# Revit family: M_螢光燈管槽 - 晶體狀
name_source: partatom
category: Leuchten
revit_build: Autodesk Revit 2017 (Build: 20160109_1515(x64)
units: mm (PartAtom-declared; Revit-internal decimal feet)

## family parameters
Basisbauteil = Fläche
Beim Laden mit Abzugskörper schneiden = Nein
Bemaßung runder Anschluss = Durchmesser verwenden
Gemeinsam genutzt = Nein
Lichtquelle = Ja
OmniClass-Nummer = 23.80.70.11.14.11
OmniClass-Titel = Downlights
Raumberechnungspunkt = Nein
Teiletyp = Normal

## types (10) — shared parameters
Emissionsform beim Rendern sichtbar = Nein
Farbfilter = 16777215
Farbtemperaturverschiebung bei Dämpfen der Lampe = <Keine Auswahl>
Lampe = T-12
Neigungswinkel = -90.00°
Vorgabe-Ansicht = 1200 mm  [stored 3.93701 ft]
分佈口材料 = 玻璃，白色，高亮度
燈箱材料 = 鋼，鍍鉻
穩壓器極數 = 1
箱高度 = 150 mm
負載分類 = 照明 - 住宅單元

## per-type parameters (varying)
| type | Baugruppenkennzeichen | Datei für fotometrisches Netz | Scheinlast | Von Breite des Rechtecks ausssenden | Von Länge des Rechtecks aussenden | 圓半徑 | 圓直徑 | 方塊寬度 | 穩壓器電壓 | 箱長度 |
| 0300x1200mm (2 燈) - 120V | D5020210 | 1x42T12.ies | 80 VA | 250 mm  [stored 0.82021 ft] | 1150 mm | 90 mm  [stored 0.295276 ft] | 180 mm  [stored 0.590551 ft] | 300 mm  [stored 0.984252 ft] | 120 V | 1200 mm  [stored 3.93701 ft] |
| 0300x1200mm (2 燈) - 277V | D5020210 | 1x42T12.ies | 80 VA | 250 mm  [stored 0.82021 ft] | 1150 mm | 90 mm  [stored 0.295276 ft] | 180 mm  [stored 0.590551 ft] | 300 mm  [stored 0.984252 ft] | 277 V | 1200 mm  [stored 3.93701 ft] |
| 0600x0600mm (2 燈) - 120V | D5020210 | 2x22T12.ies | 40 VA | 550 mm | 550 mm | 180 mm  [stored 0.590551 ft] | 360 mm  [stored 1.1811 ft] | 600 mm  [stored 1.9685 ft] | 120 V | 600 mm  [stored 1.9685 ft] |
| 0600x0600mm (2 燈) - 277V | D5020210 | 2x22T12.ies | 40 VA | 550 mm | 550 mm | 180 mm  [stored 0.590551 ft] | 360 mm  [stored 1.1811 ft] | 600 mm  [stored 1.9685 ft] | 277 V | 600 mm  [stored 1.9685 ft] |
| 0600x0600mm (4 燈) - 120V | D5020210 | 2x24T12.ies | 80 VA | 550 mm | 550 mm | 180 mm  [stored 0.590551 ft] | 360 mm  [stored 1.1811 ft] | 600 mm  [stored 1.9685 ft] | 120 V | 600 mm  [stored 1.9685 ft] |
| 0600x0600mm (4 燈) - 277V | D5020210 | 2x24T12.ies | 80 VA | 550 mm | 550 mm | 180 mm  [stored 0.590551 ft] | 360 mm  [stored 1.1811 ft] | 600 mm  [stored 1.9685 ft] | 277 V | 600 mm  [stored 1.9685 ft] |
| 0600x1200mm (2 燈) - 120V | D5020210 | 2x42T12.ies | 80 VA | 550 mm | 1150 mm | 180 mm  [stored 0.590551 ft] | 360 mm  [stored 1.1811 ft] | 600 mm  [stored 1.9685 ft] | 120 V | 1200 mm  [stored 3.93701 ft] |
| 0600x1200mm (2 燈) - 277V |  | 2x42T12.ies | 80 VA | 550 mm | 1150 mm | 180 mm  [stored 0.590551 ft] | 360 mm  [stored 1.1811 ft] | 600 mm  [stored 1.9685 ft] | 277 V | 1200 mm  [stored 3.93701 ft] |
| 0600x1200mm (4 燈) - 120V | D5020210 | 2x44T12.ies | 160 VA | 550 mm | 1150 mm | 180 mm  [stored 0.590551 ft] | 360 mm  [stored 1.1811 ft] | 600 mm  [stored 1.9685 ft] | 120 V | 1200 mm  [stored 3.93701 ft] |
| 0600x1200mm (4 燈) - 277V | D5020210 | 2x44T12.ies | 160 VA | 550 mm | 1150 mm | 180 mm  [stored 0.590551 ft] | 360 mm  [stored 1.1811 ft] | 600 mm  [stored 1.9685 ft] | 277 V | 1200 mm  [stored 3.93701 ft] |

note: [stored X ft] marks values corroborated as IEEE doubles in the binary element streams (Revit-internal decimal feet)
